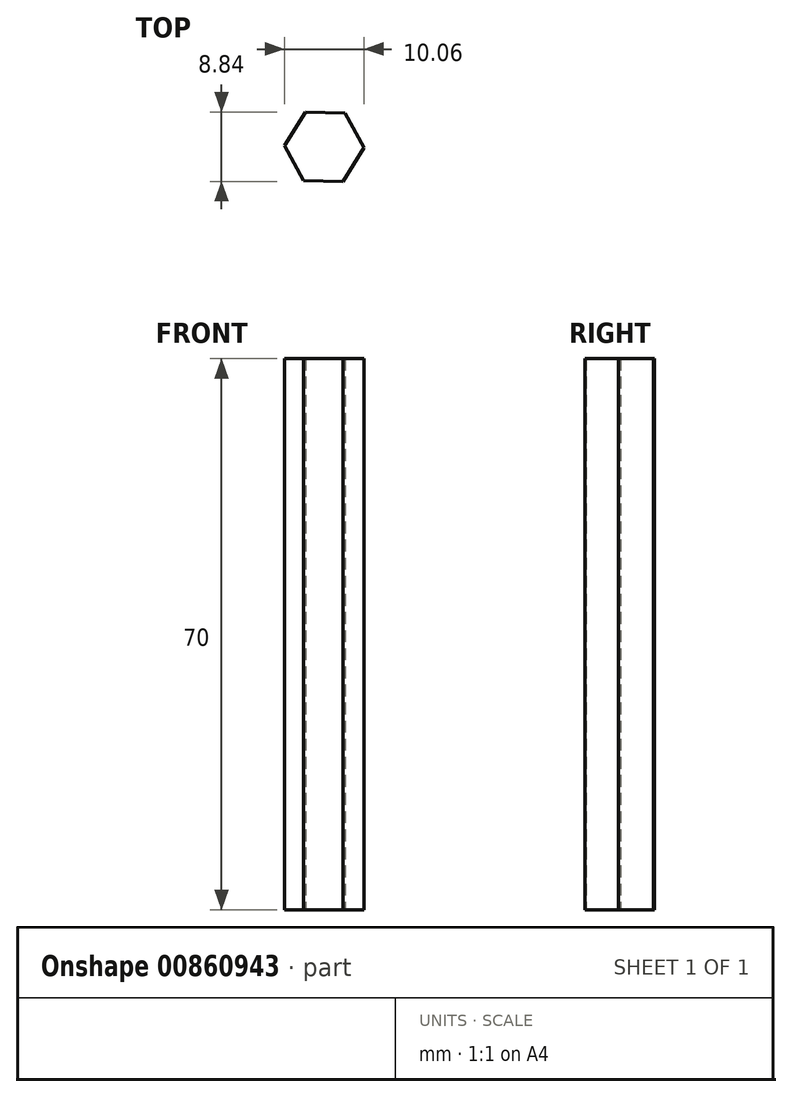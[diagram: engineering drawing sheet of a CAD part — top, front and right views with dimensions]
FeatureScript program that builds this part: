
annotation { "Feature Type Name" : "Feature", "Feature Type Description" : "" }
export const myFeature = defineFeature(function(context is Context, id is Id, definition is map)
    precondition{}
    {
        {
            var Q0;
            Q0=qCreatedBy(makeId("Top.planeOp"),FACE);
            var sketch = newSketch(context, id + "F0", { "sketchPlane" : qUnion([Q0])});
            skCircle(sketch, "E0.cCircle", {"center": v(0, 0) * mm, "radius": 4.36 * mm, "construction": true});
            skLineSegment(sketch, "E0.0", {"start": v(5.03, -0.12) * mm, "end": v(2.41, -4.42) * mm});
            skLineSegment(sketch, "E0.1", {"start": v(2.41, -4.42) * mm, "end": v(-2.62, -4.3) * mm});
            skLineSegment(sketch, "E0.2", {"start": v(-2.62, -4.3) * mm, "end": v(-5.03, 0.12) * mm});
            skLineSegment(sketch, "E0.3", {"start": v(-5.03, 0.12) * mm, "end": v(-2.41, 4.42) * mm});
            skLineSegment(sketch, "E0.4", {"start": v(-2.41, 4.42) * mm, "end": v(2.62, 4.3) * mm});
            skLineSegment(sketch, "E0.5", {"start": v(2.62, 4.3) * mm, "end": v(5.03, -0.12) * mm});
            skPoint(sketch, "E0.0.midPoint", {"position": v(3.72, -2.27) * mm});
            skSolve(sketch);
        }
        {
            var Q0;
            Q0 = qSketchRegion(id + "F0", true);
            extrude(context, id + "F1", {"entities" : qUnion([Q0]), "depth" : 70 * mm, "offsetDistance" : 25 * mm});
        }
    });
